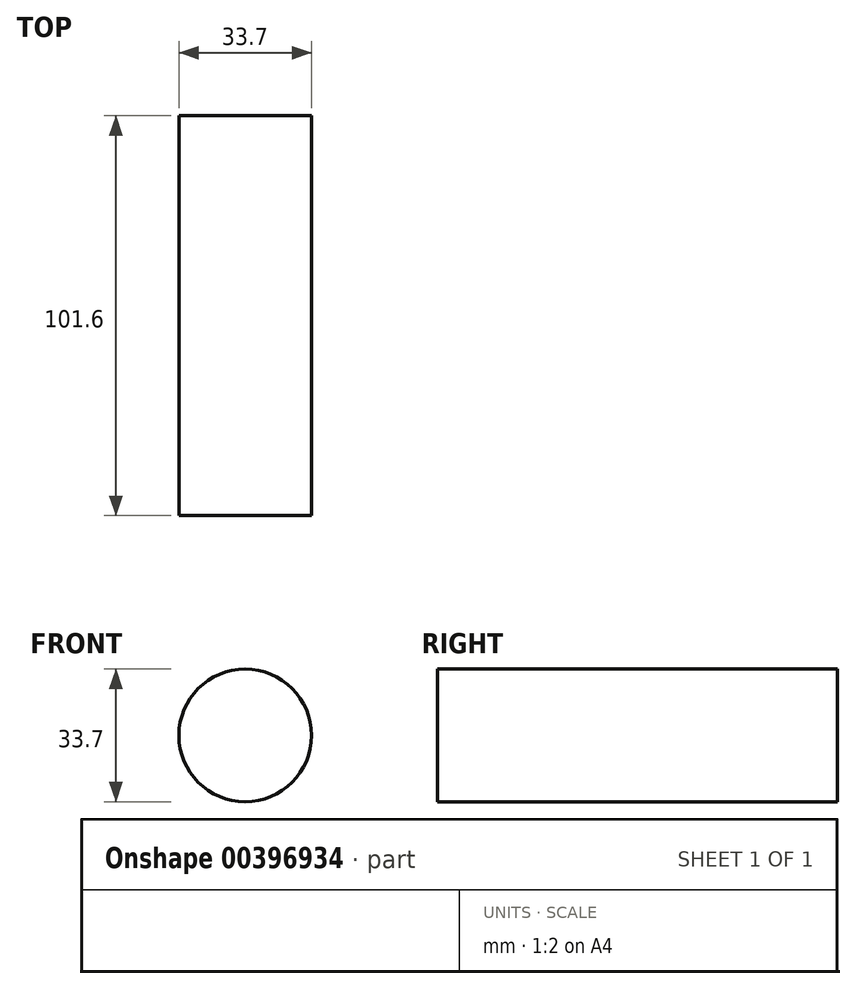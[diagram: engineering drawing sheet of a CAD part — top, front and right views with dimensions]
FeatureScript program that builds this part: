
annotation { "Feature Type Name" : "Feature", "Feature Type Description" : "" }
export const myFeature = defineFeature(function(context is Context, id is Id, definition is map)
    precondition{}
    {
        {
            var Q0;
            Q0=qCreatedBy(makeId("Front.planeOp"),FACE);
            var sketch = newSketch(context, id + "F0", { "sketchPlane" : qUnion([Q0])});
            skCircle(sketch, "E0", {"center": v(0, 0) * mm, "radius": 16.85 * mm});
            skSolve(sketch);
        }
        {
            var Q0;
            Q0=makeQuery(id+"F0.imprint","IMPRINT",FACE,{"disambiguationData":[TD([[makeQuery(id+"F0.imprint","IMPRINT",EDGE,{"derivedFrom":sQuery(id+"F0.wireOp",EDGE,"E0")}),1.0]])]});
            extrude(context, id + "F1", {"entities" : qUnion([Q0]), "depth" : 101.6 * mm});
        }
    });
